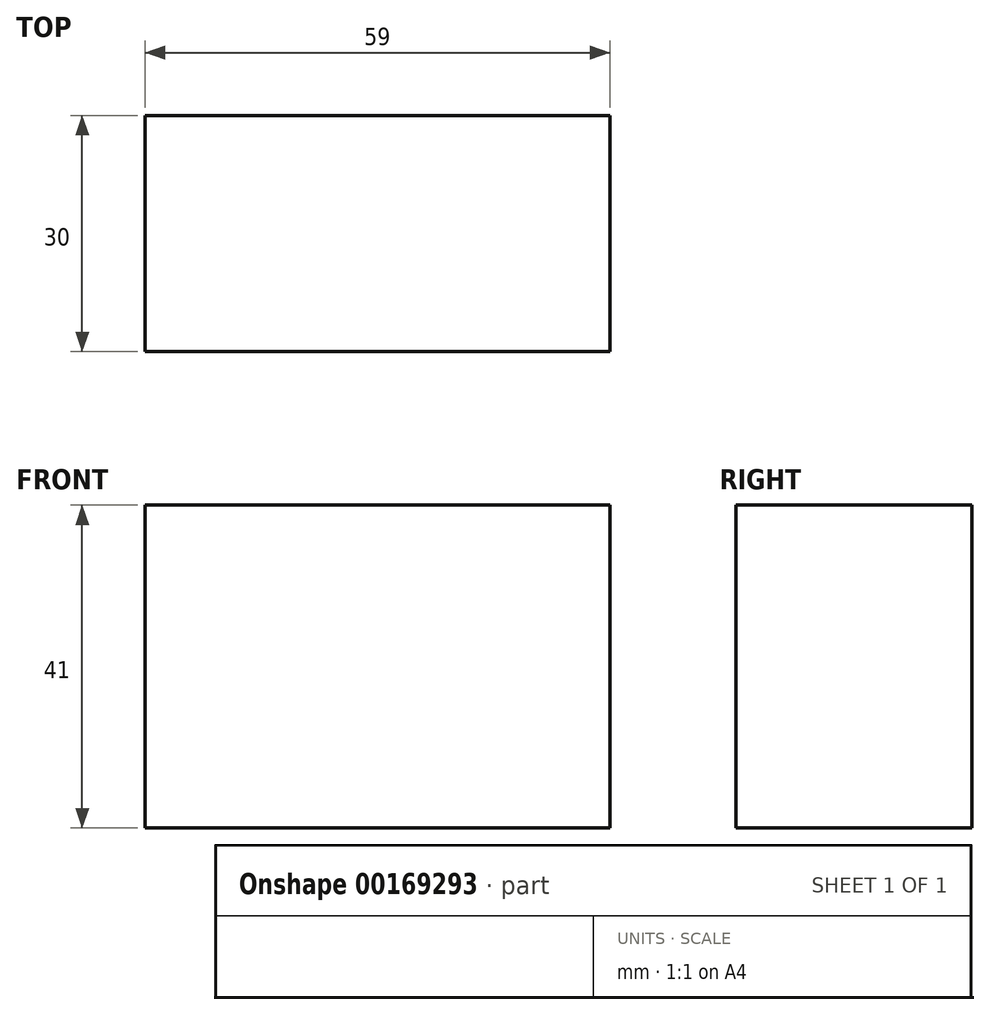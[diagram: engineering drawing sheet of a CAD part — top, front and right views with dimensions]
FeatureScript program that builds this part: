
annotation { "Feature Type Name" : "Feature", "Feature Type Description" : "" }
export const myFeature = defineFeature(function(context is Context, id is Id, definition is map)
    precondition{}
    {
        {
            var Q0;
            Q0=qCreatedBy(makeId("Front.planeOp"),FACE);
            var sketch = newSketch(context, id + "F0", { "sketchPlane" : qUnion([Q0])});
            skLineSegment(sketch, "E0.bottom", {"start": v(29.5, 20.5) * mm, "end": v(-29.5, 20.5) * mm});
            skLineSegment(sketch, "E0.top", {"start": v(29.5, -20.5) * mm, "end": v(-29.5, -20.5) * mm});
            skLineSegment(sketch, "E0.left", {"start": v(29.5, 20.5) * mm, "end": v(29.5, -20.5) * mm});
            skLineSegment(sketch, "E0.right", {"start": v(-29.5, 20.5) * mm, "end": v(-29.5, -20.5) * mm});
            skPoint(sketch, "E0.middle", {"position": v(0, 0) * mm});
            skSolve(sketch);
        }
        {
            var Q0;
            Q0 = qSketchRegion(id + "F0", true);
            extrude(context, id + "F1", {"entities" : qUnion([Q0]), "depth" : 30 * mm});
        }
    });
